# Revit family: STS-182А_RV17_LOD400 (06.11.23)
name_source: partatom
category: Электрооборудование
revit_build: Autodesk Revit 2017 (Build: 20170118_1100(x64)
units: mm (PartAtom-declared; Revit-internal decimal feet)

## family parameters
Всегда вертикально = Нет
Конфигурация панели = Два столбца, слева направо
На основе рабочей плоскости = Нет
Общий = Нет
При загрузке вырезать с полостями = Нет
Размер круглого соединителя = Использовать диаметр
Тип детали = Щит
Точка расчета площади = Нет

## types (1)
- STS-182А
    ADSK_URL страницы изделия = https://stilsoft.ru
    ADSK_Единица измерения = шт.
    ADSK_Завод-изготовитель = ООО «Основа Безопасности»
    ADSK_Количество = 10
    ADSK_Марка = СТВФ.426471.143
    ADSK_Масса = 0.25
    ADSK_Наименование = Коммутатор STS-182А
    d_короба = 0 мм
    Вариант исполнения = уличное
    Время непрерывной работы, ч = круглосуточно
    Диапазон рабочих температур, = от -40 до +55
    Длина физического сегмента, не менее, м = 100 мм
    Максимальная скорость передачи, до Мбит/с = 100
    Мощность = 2
    Напряжение электропитания, В = Active PoE IEEE802.3af и IEEE802.3at
